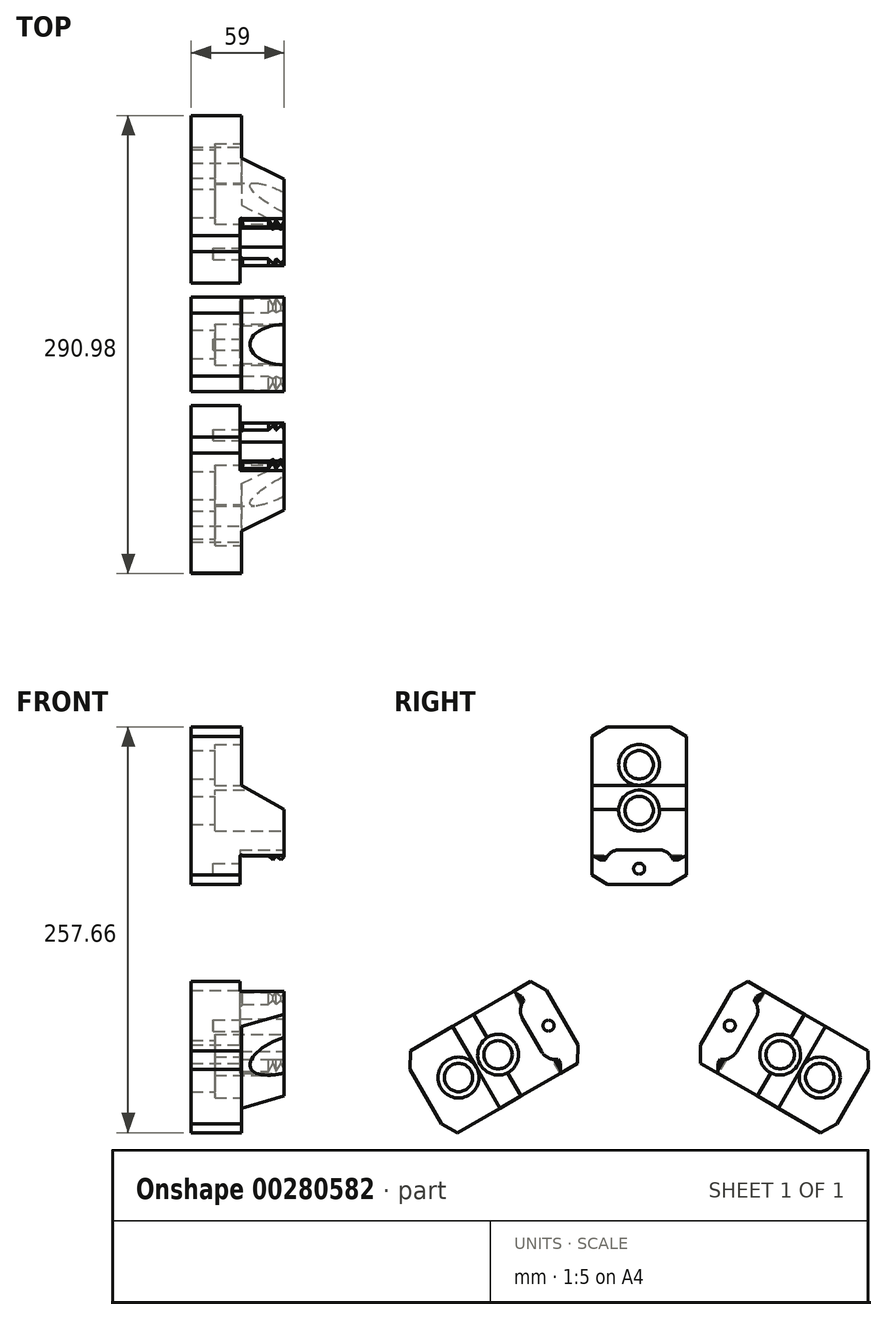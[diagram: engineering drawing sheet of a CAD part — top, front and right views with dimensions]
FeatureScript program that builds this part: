
annotation { "Feature Type Name" : "Feature", "Feature Type Description" : "" }
export const myFeature = defineFeature(function(context is Context, id is Id, definition is map)
    precondition{}
    {
        {
            var Q0;
            Q0=qCreatedBy(makeId("Front.planeOp"),FACE);
            var sketch = newSketch(context, id + "F0", { "sketchPlane" : qUnion([Q0])});
            skLineSegment(sketch, "E0", {"start": v(3, 56.45) * mm, "end": v(3, 156.45) * mm});
            skLineSegment(sketch, "E1", {"start": v(3, 156.45) * mm, "end": v(35, 156.45) * mm});
            skLineSegment(sketch, "E2", {"start": v(35, 156.45) * mm, "end": v(35, 119.45) * mm});
            skLineSegment(sketch, "E3", {"start": v(35, 119.45) * mm, "end": v(62, 104) * mm});
            skLineSegment(sketch, "E4", {"start": v(62, 104) * mm, "end": v(62, 74) * mm});
            skLineSegment(sketch, "E5", {"start": v(3, 56.45) * mm, "end": v(34, 56.45) * mm});
            skLineSegment(sketch, "E6", {"start": v(34, 56.45) * mm, "end": v(34, 74.45) * mm});
            skLineSegment(sketch, "E7", {"start": v(52, 74.45) * mm, "end": v(55, 72) * mm});
            skLineSegment(sketch, "E8", {"start": v(55, 72) * mm, "end": v(57, 74.45) * mm});
            skLineSegment(sketch, "E9", {"start": v(57, 74.45) * mm, "end": v(60, 72) * mm});
            skLineSegment(sketch, "E10", {"start": v(60, 72) * mm, "end": v(62, 74) * mm});
            skArc(sketch, "E11", {"start": v(35.5, 74.45) * mm, "mid": v(34.75, 75.2) * mm, "end": v(34, 74.45) * mm});
            skLineSegment(sketch, "E12.trimOffspring", {"start": v(35.5, 74.45) * mm, "end": v(52, 74.45) * mm});
            skLineSegment(sketch, "E13", {"start": v(0, 0) * mm, "end": v(70.08, 0) * mm, "construction": true});
            skSolve(sketch);
        }
        {
            var Q0;
            Q0 = qSketchRegion(id + "F0", true);
            extrude(context, id + "F1", {"entities" : qUnion([Q0]), "depth" : 60 * mm, "symmetric" : true});
        }
        {
            var Q0;
            Q0=makeQuery(id+"F1.opExtrude","SWEPT_FACE",FACE,{"disambiguationData":[OSD([sQuery(id+"F0.wireOp",EDGE,"E2")])]});
            var sketch = newSketch(context, id + "F2", { "sketchPlane" : qUnion([Q0])});
            skLineSegment(sketch, "E14", {"start": v(20, 156.45) * mm, "end": v(30, 150.45) * mm});
            skLineSegment(sketch, "E15", {"start": v(30, 150.45) * mm, "end": v(30, 156.45) * mm});
            skLineSegment(sketch, "E16", {"start": v(30, 156.45) * mm, "end": v(20, 156.45) * mm});
            skLineSegment(sketch, "E17", {"start": v(20, 56.45) * mm, "end": v(30, 62.45) * mm});
            skLineSegment(sketch, "E18", {"start": v(30, 62.45) * mm, "end": v(30, 56.45) * mm});
            skLineSegment(sketch, "E19", {"start": v(30, 56.45) * mm, "end": v(20, 56.45) * mm});
            skLineSegment(sketch, "E20", {"start": v(0, 42.7) * mm, "end": v(0, 168.17) * mm, "construction": true});
            skLineSegment(sketch, "E21.MirrorCS", {"start": v(-20, 156.45) * mm, "end": v(-30, 150.45) * mm});
            skLineSegment(sketch, "E22.MirrorCS", {"start": v(-30, 156.45) * mm, "end": v(-20, 156.45) * mm});
            skLineSegment(sketch, "E23.MirrorCS", {"start": v(-30, 150.45) * mm, "end": v(-30, 156.45) * mm});
            skLineSegment(sketch, "E24.MirrorCS", {"start": v(-20, 56.45) * mm, "end": v(-30, 62.45) * mm});
            skLineSegment(sketch, "E25.MirrorCS", {"start": v(-30, 62.45) * mm, "end": v(-30, 56.45) * mm});
            skLineSegment(sketch, "E26.MirrorCS", {"start": v(-30, 56.45) * mm, "end": v(-20, 56.45) * mm});
            skSolve(sketch);
        }
        {
            var Q0;
            Q0=makeQuery(id+"F2.imprint","IMPRINT",FACE,{"disambiguationData":[TD([[makeQuery(id+"F2.imprint","IMPRINT",EDGE,{"derivedFrom":sQuery(id+"F2.wireOp",EDGE,"E21.MirrorCS")}),-1.0]])]});
            var Q1;
            Q1=makeQuery(id+"F2.imprint","IMPRINT",FACE,{"disambiguationData":[TD([[makeQuery(id+"F2.imprint","IMPRINT",EDGE,{"derivedFrom":sQuery(id+"F2.wireOp",EDGE,"E14")}),1.0]])]});
            var Q2;
            Q2=makeQuery(id+"F2.imprint","IMPRINT",FACE,{"disambiguationData":[TD([[makeQuery(id+"F2.imprint","IMPRINT",EDGE,{"derivedFrom":sQuery(id+"F2.wireOp",EDGE,"E17")}),-1.0]])]});
            var Q3;
            Q3=makeQuery(id+"F2.imprint","IMPRINT",FACE,{"disambiguationData":[TD([[makeQuery(id+"F2.imprint","IMPRINT",EDGE,{"derivedFrom":sQuery(id+"F2.wireOp",EDGE,"E24.MirrorCS")}),1.0]])]});
            var Q4;
            Q4=makeQuery(id+"F1.opExtrude","SWEPT_FACE",FACE,{"disambiguationData":[OSD([sQuery(id+"F0.wireOp",EDGE,"E0")])]});
            extrude(context, id + "F3", {"entities" : qUnion([Q0, Q1, Q2, Q3]), "operationType" : NewBodyOperationType.REMOVE, "endBound" : BoundingType.UP_TO_SURFACE, "oppositeDirection" : true, "endBoundEntityFace" : qUnion([Q4]), "depth" : 25 * mm});
        }
        {
            var Q0;
            Q0=makeQuery(id+"F1.opExtrude","SWEPT_FACE",FACE,{"disambiguationData":[OSD([sQuery(id+"F0.wireOp",EDGE,"E4")])]});
            var sketch = newSketch(context, id + "F4", { "sketchPlane" : qUnion([Q0])});
            skLineSegment(sketch, "E27", {"start": v(30, 75) * mm, "end": v(24.5, 72) * mm});
            skLineSegment(sketch, "E28", {"start": v(24.5, 72) * mm, "end": v(30, 72) * mm});
            skLineSegment(sketch, "E29", {"start": v(30, 72) * mm, "end": v(30, 75) * mm});
            skLineSegment(sketch, "E30", {"start": v(0, 67.05) * mm, "end": v(0, 113.15) * mm, "construction": true});
            skPoint(sketch, "E30.endSnap0", {"position": v(0, 104) * mm});
            skLineSegment(sketch, "E31.MirrorCS", {"start": v(-30, 75) * mm, "end": v(-24.5, 72) * mm});
            skLineSegment(sketch, "E32.MirrorCS", {"start": v(-30, 72) * mm, "end": v(-30, 75) * mm});
            skLineSegment(sketch, "E33.MirrorCS", {"start": v(-24.5, 72) * mm, "end": v(-30, 72) * mm});
            skSolve(sketch);
        }
        {
            var Q0;
            {var subQ0=sQuery(id+"F4.wireOp",EDGE,"E33.MirrorCS");Q0=makeQuery(id+"F4.imprint","IMPRINT",FACE,{"disambiguationData":[TD([[makeQuery(id+"F4.imprint","IMPRINT",EDGE,{"derivedFrom":subQ0}),-1.0]])]});}
            var Q1;
            {var subQ0=sQuery(id+"F4.wireOp",EDGE,"E32.MirrorCS");var subQ1=sQuery(id+"F4.wireOp",EDGE,"E31.MirrorCS");var subQ2=sQuery(id+"F0.wireOp",EDGE,"E4");var subQ3=makeQuery(id+"F4.imprint","INTERSECT",VERTEX,{"derivedFrom":[makeQuery(id+"F1.opExtrude","CAP_EDGE",EDGE,{"disambiguationData":[OSD([subQ2])],"isStart":false}),subQ1,subQ0]});Q1=makeQuery(id+"F4.imprint","IMPRINT",FACE,{"disambiguationData":[TD([[makeQuery(id+"F4.imprint","IMPRINT",EDGE,{"disambiguationData":[TD([[subQ3,-1.0]])],"derivedFrom":subQ1}),-1.0]])]});}
            var Q2;
            {var subQ0=sQuery(id+"F4.wireOp",EDGE,"E29");var subQ1=sQuery(id+"F4.wireOp",EDGE,"E27");var subQ2=sQuery(id+"F0.wireOp",EDGE,"E4");var subQ3=makeQuery(id+"F4.imprint","INTERSECT",VERTEX,{"derivedFrom":[makeQuery(id+"F1.opExtrude","CAP_EDGE",EDGE,{"disambiguationData":[OSD([subQ2])],"isStart":true}),subQ1,subQ0]});Q2=makeQuery(id+"F4.imprint","IMPRINT",FACE,{"disambiguationData":[TD([[makeQuery(id+"F4.imprint","IMPRINT",EDGE,{"disambiguationData":[TD([[subQ3,-1.0]])],"derivedFrom":subQ1}),1.0]])]});}
            var Q3;
            {var subQ0=sQuery(id+"F4.wireOp",EDGE,"E28");Q3=makeQuery(id+"F4.imprint","IMPRINT",FACE,{"disambiguationData":[TD([[makeQuery(id+"F4.imprint","IMPRINT",EDGE,{"derivedFrom":subQ0}),1.0]])]});}
            var Q4;
            Q4=makeQuery(id+"F1.opExtrude","SWEPT_FACE",FACE,{"disambiguationData":[OSD([sQuery(id+"F0.wireOp",EDGE,"E6")])]});
            extrude(context, id + "F5", {"entities" : qUnion([Q0, Q1, Q2, Q3]), "operationType" : NewBodyOperationType.REMOVE, "endBound" : BoundingType.UP_TO_SURFACE, "oppositeDirection" : true, "endBoundEntityFace" : qUnion([Q4]), "depth" : 27.7 * mm});
        }
        {
            var Q0;
            Q0=makeQuery(id+"F1.opExtrude","SWEPT_FACE",FACE,{"disambiguationData":[OSD([sQuery(id+"F0.wireOp",EDGE,"E4")])]});
            var sketch = newSketch(context, id + "F6", { "sketchPlane" : qUnion([Q0])});
            skLineSegment(sketch, "E34", {"start": v(0, 70.5) * mm, "end": v(0, 96.88) * mm, "construction": true});
            skPoint(sketch, "E34.startSnap0", {"position": v(0, 74) * mm});
            skLineSegment(sketch, "E35", {"start": v(12.26, 78.5) * mm, "end": v(0, 78.5) * mm});
            skLineSegment(sketch, "E36", {"start": v(21.5, 72) * mm, "end": v(0, 72) * mm});
            skPoint(sketch, "E37", {"position": v(12, 78.5) * mm});
            skArc(sketch, "E38", {"start": v(21.5, 72) * mm, "mid": v(17.78, 76.75) * mm, "end": v(12, 78.5) * mm});
            skPoint(sketch, "E39.end.orphan", {"position": v(21.5, 78.5) * mm});
            skLineSegment(sketch, "E40.MirrorCS", {"start": v(-12.26, 78.5) * mm, "end": v(0, 78.5) * mm});
            skArc(sketch, "E41.MirrorCS", {"start": v(-21.5, 72) * mm, "mid": v(-17.78, 76.75) * mm, "end": v(-12, 78.5) * mm});
            skLineSegment(sketch, "E42.MirrorCS", {"start": v(-21.5, 72) * mm, "end": v(0, 72) * mm});
            skSolve(sketch);
        }
        {
            var Q0;
            Q0 = qSketchRegion(id + "F6", true);
            var Q1;
            Q1=makeQuery(id+"F5.boolean.opBoolean","MERGE",FACE,{"derivedFrom":[makeQuery(id+"F1.opExtrude","SWEPT_FACE",FACE,{"disambiguationData":[OSD([sQuery(id+"F0.wireOp",EDGE,"E6")])]})],"fromTools":[makeQuery(id+"F5.opExtrude","CAP_FACE",FACE,{"disambiguationData":[OSD([sQuery(id+"F4.wireOp",EDGE,"E27"),sQuery(id+"F4.wireOp",EDGE,"E28"),sQuery(id+"F4.wireOp",EDGE,"E29")])],"isStart":false}),makeQuery(id+"F5.opExtrude","CAP_FACE",FACE,{"disambiguationData":[OSD([sQuery(id+"F4.wireOp",EDGE,"E31.MirrorCS"),sQuery(id+"F4.wireOp",EDGE,"E32.MirrorCS"),sQuery(id+"F4.wireOp",EDGE,"E33.MirrorCS")])],"isStart":false})]});
            extrude(context, id + "F7", {"entities" : qUnion([Q0]), "operationType" : NewBodyOperationType.REMOVE, "endBound" : BoundingType.UP_TO_SURFACE, "oppositeDirection" : true, "endBoundEntityFace" : qUnion([Q1]), "depth" : 25 * mm});
        }
        {
            var Q0;
            Q0=makeQuery(id+"F7.boolean.opBoolean","MERGE",FACE,{"derivedFrom":[makeQuery(id+"F5.boolean.opBoolean","MERGE",FACE,{"derivedFrom":[makeQuery(id+"F1.opExtrude","SWEPT_FACE",FACE,{"disambiguationData":[OSD([sQuery(id+"F0.wireOp",EDGE,"E6")])]})],"fromTools":[makeQuery(id+"F5.opExtrude","CAP_FACE",FACE,{"disambiguationData":[OSD([sQuery(id+"F4.wireOp",EDGE,"E27"),sQuery(id+"F4.wireOp",EDGE,"E28"),sQuery(id+"F4.wireOp",EDGE,"E29")])],"isStart":false}),makeQuery(id+"F5.opExtrude","CAP_FACE",FACE,{"disambiguationData":[OSD([sQuery(id+"F4.wireOp",EDGE,"E31.MirrorCS"),sQuery(id+"F4.wireOp",EDGE,"E32.MirrorCS"),sQuery(id+"F4.wireOp",EDGE,"E33.MirrorCS")])],"isStart":false})]})],"fromTools":[makeQuery(id+"F7.opExtrude","CAP_FACE",FACE,{"disambiguationData":[OSD([sQuery(id+"F6.wireOp",EDGE,"E35"),sQuery(id+"F6.wireOp",EDGE,"E36"),sQuery(id+"F6.wireOp",EDGE,"E38"),sQuery(id+"F6.wireOp",EDGE,"E40.MirrorCS"),sQuery(id+"F6.wireOp",EDGE,"E41.MirrorCS"),sQuery(id+"F6.wireOp",EDGE,"E42.MirrorCS")])],"isStart":false})]});
            var sketch = newSketch(context, id + "F8", { "sketchPlane" : qUnion([Q0])});
            skCircle(sketch, "E43.cCircle", {"center": v(0, 66.45) * mm, "radius": 6.5 * mm, "construction": true});
            skLineSegment(sketch, "E43.0", {"start": v(7.5, 66.45) * mm, "end": v(3.75, 59.95) * mm});
            skLineSegment(sketch, "E43.1", {"start": v(3.75, 59.95) * mm, "end": v(-3.75, 59.95) * mm});
            skLineSegment(sketch, "E43.2", {"start": v(-3.75, 59.95) * mm, "end": v(-7.5, 66.45) * mm});
            skLineSegment(sketch, "E43.3", {"start": v(-7.5, 66.45) * mm, "end": v(-3.75, 72.95) * mm});
            skLineSegment(sketch, "E43.4", {"start": v(-3.75, 72.95) * mm, "end": v(3.75, 72.95) * mm});
            skLineSegment(sketch, "E43.5", {"start": v(3.75, 72.95) * mm, "end": v(7.5, 66.45) * mm});
            skPoint(sketch, "E43.0.midPoint", {"position": v(5.63, 63.2) * mm});
            skCircle(sketch, "E44", {"center": v(0, 66.45) * mm, "radius": 3.5 * mm});
            skSolve(sketch);
        }
        {
            var Q0;
            Q0=makeQuery(id+"F8.imprint","IMPRINT",FACE,{"disambiguationData":[TD([[makeQuery(id+"F8.imprint","IMPRINT",EDGE,{"derivedFrom":sQuery(id+"F8.wireOp",EDGE,"E44")}),1.0]])]});
            extrude(context, id + "F9", {"entities" : qUnion([Q0]), "operationType" : NewBodyOperationType.REMOVE, "oppositeDirection" : true, "depth" : 17 * mm});
        }
        {
            var Q0;
            Q0=makeQuery(id+"F1.opExtrude","SWEPT_FACE",FACE,{"disambiguationData":[OSD([sQuery(id+"F0.wireOp",EDGE,"E4")])]});
            var sketch = newSketch(context, id + "F10", { "sketchPlane" : qUnion([Q0])});
            skLineSegment(sketch, "E45", {"start": v(0, 77.6) * mm, "end": v(0, 164.13) * mm, "construction": true});
            skPoint(sketch, "E45.startSnap0", {"position": v(0, 78.5) * mm});
            skCircle(sketch, "E46", {"center": v(0, 132.45) * mm, "radius": 13 * mm});
            skCircle(sketch, "E47", {"center": v(0, 103.45) * mm, "radius": 13 * mm});
            skCircle(sketch, "E48", {"center": v(0, 132.45) * mm, "radius": 9 * mm});
            skCircle(sketch, "E49", {"center": v(0, 103.45) * mm, "radius": 9 * mm});
            skSolve(sketch);
        }
        {
            var Q0;
            Q0=makeQuery(id+"F10.imprint","IMPRINT",FACE,{"disambiguationData":[TD([[makeQuery(id+"F10.imprint","IMPRINT",EDGE,{"derivedFrom":sQuery(id+"F10.wireOp",EDGE,"E48")}),1.0]])]});
            var Q1;
            {var subQ0=sQuery(id+"F10.wireOp",EDGE,"E49");var subQ1=makeQuery(id+"F1.opExtrude","SWEPT_EDGE",EDGE,{"disambiguationData":[OSD([sQuery(id+"F0.wireOp",EDGE,"E3"),sQuery(id+"F0.wireOp",EDGE,"E4")])]});var subQ2=makeQuery(id+"F10.imprint","INTERSECT",VERTEX,{"disambiguationData":[OD(0.0)],"derivedFrom":[subQ1,subQ0]});Q1=makeQuery(id+"F10.imprint","IMPRINT",FACE,{"disambiguationData":[TD([[makeQuery(id+"F10.imprint","IMPRINT",EDGE,{"disambiguationData":[TD([[subQ2,1.0]])],"derivedFrom":subQ0}),1.0]])]});}
            var Q2;
            {var subQ0=sQuery(id+"F10.wireOp",EDGE,"E49");var subQ1=makeQuery(id+"F1.opExtrude","SWEPT_EDGE",EDGE,{"disambiguationData":[OSD([sQuery(id+"F0.wireOp",EDGE,"E3"),sQuery(id+"F0.wireOp",EDGE,"E4")])]});var subQ2=makeQuery(id+"F10.imprint","INTERSECT",VERTEX,{"disambiguationData":[OD(0.0)],"derivedFrom":[subQ1,subQ0]});Q2=makeQuery(id+"F10.imprint","IMPRINT",FACE,{"disambiguationData":[TD([[makeQuery(id+"F10.imprint","IMPRINT",EDGE,{"disambiguationData":[TD([[subQ2,-1.0]])],"derivedFrom":subQ0}),1.0]])]});}
            var Q3;
            Q3=makeQuery(id+"F1.opExtrude","SWEPT_FACE",FACE,{"disambiguationData":[OSD([sQuery(id+"F0.wireOp",EDGE,"E0")])]});
            extrude(context, id + "F11", {"entities" : qUnion([Q0, Q1, Q2]), "operationType" : NewBodyOperationType.REMOVE, "endBound" : BoundingType.UP_TO_SURFACE, "oppositeDirection" : true, "endBoundEntityFace" : qUnion([Q3]), "depth" : 25 * mm});
        }
        {
            var Q0;
            Q0=makeQuery(id+"F10.imprint","IMPRINT",FACE,{"disambiguationData":[TD([[makeQuery(id+"F10.imprint","IMPRINT",EDGE,{"derivedFrom":sQuery(id+"F10.wireOp",EDGE,"E46")}),1.0]])]});
            var Q1;
            {var subQ0=sQuery(id+"F10.wireOp",EDGE,"E47");var subQ1=makeQuery(id+"F1.opExtrude","SWEPT_EDGE",EDGE,{"disambiguationData":[OSD([sQuery(id+"F0.wireOp",EDGE,"E3"),sQuery(id+"F0.wireOp",EDGE,"E4")])]});var subQ2=makeQuery(id+"F10.imprint","INTERSECT",VERTEX,{"disambiguationData":[OD(0.0)],"derivedFrom":[subQ1,subQ0]});Q1=makeQuery(id+"F10.imprint","IMPRINT",FACE,{"disambiguationData":[TD([[makeQuery(id+"F10.imprint","IMPRINT",EDGE,{"disambiguationData":[TD([[subQ2,-1.0]])],"derivedFrom":subQ0}),1.0]])]});}
            var Q2;
            {var subQ0=sQuery(id+"F10.wireOp",EDGE,"E47");var subQ1=makeQuery(id+"F1.opExtrude","SWEPT_EDGE",EDGE,{"disambiguationData":[OSD([sQuery(id+"F0.wireOp",EDGE,"E3"),sQuery(id+"F0.wireOp",EDGE,"E4")])]});var subQ2=makeQuery(id+"F10.imprint","INTERSECT",VERTEX,{"disambiguationData":[OD(0.0)],"derivedFrom":[subQ1,subQ0]});Q2=makeQuery(id+"F10.imprint","IMPRINT",FACE,{"disambiguationData":[TD([[makeQuery(id+"F10.imprint","IMPRINT",EDGE,{"disambiguationData":[TD([[subQ2,1.0]])],"derivedFrom":subQ0}),1.0]])]});}
            extrude(context, id + "F12", {"entities" : qUnion([Q0, Q1, Q2]), "operationType" : NewBodyOperationType.REMOVE, "oppositeDirection" : true, "depth" : 44 * mm});
        }
        {
            var Q0;
            Q0=makeQuery(id+"F1.opExtrude","SWEPT_BODY",BODY,{"disambiguationData":[OSD([sQuery(id+"F0.wireOp",EDGE,"E0"),sQuery(id+"F0.wireOp",EDGE,"E1"),sQuery(id+"F0.wireOp",EDGE,"E2"),sQuery(id+"F0.wireOp",EDGE,"E3"),sQuery(id+"F0.wireOp",EDGE,"E4"),sQuery(id+"F0.wireOp",EDGE,"E5"),sQuery(id+"F0.wireOp",EDGE,"E6"),sQuery(id+"F0.wireOp",EDGE,"E7"),sQuery(id+"F0.wireOp",EDGE,"E8"),sQuery(id+"F0.wireOp",EDGE,"E9"),sQuery(id+"F0.wireOp",EDGE,"E10"),sQuery(id+"F0.wireOp",EDGE,"E11"),sQuery(id+"F0.wireOp",EDGE,"E12.trimOffspring")])]});
            var Q1;
            Q1=sQuery(id+"F0.wireOp",EDGE,"E13");
            circularPattern(context, id + "F13", {"entities" : qUnion([Q0]), "axis" : qUnion([Q1]), "angle" : 360 * degree, "instanceCount" : 3, "equalSpace" : true, "computeTransformsWithoutBuiltin" : true});
        }
    });
